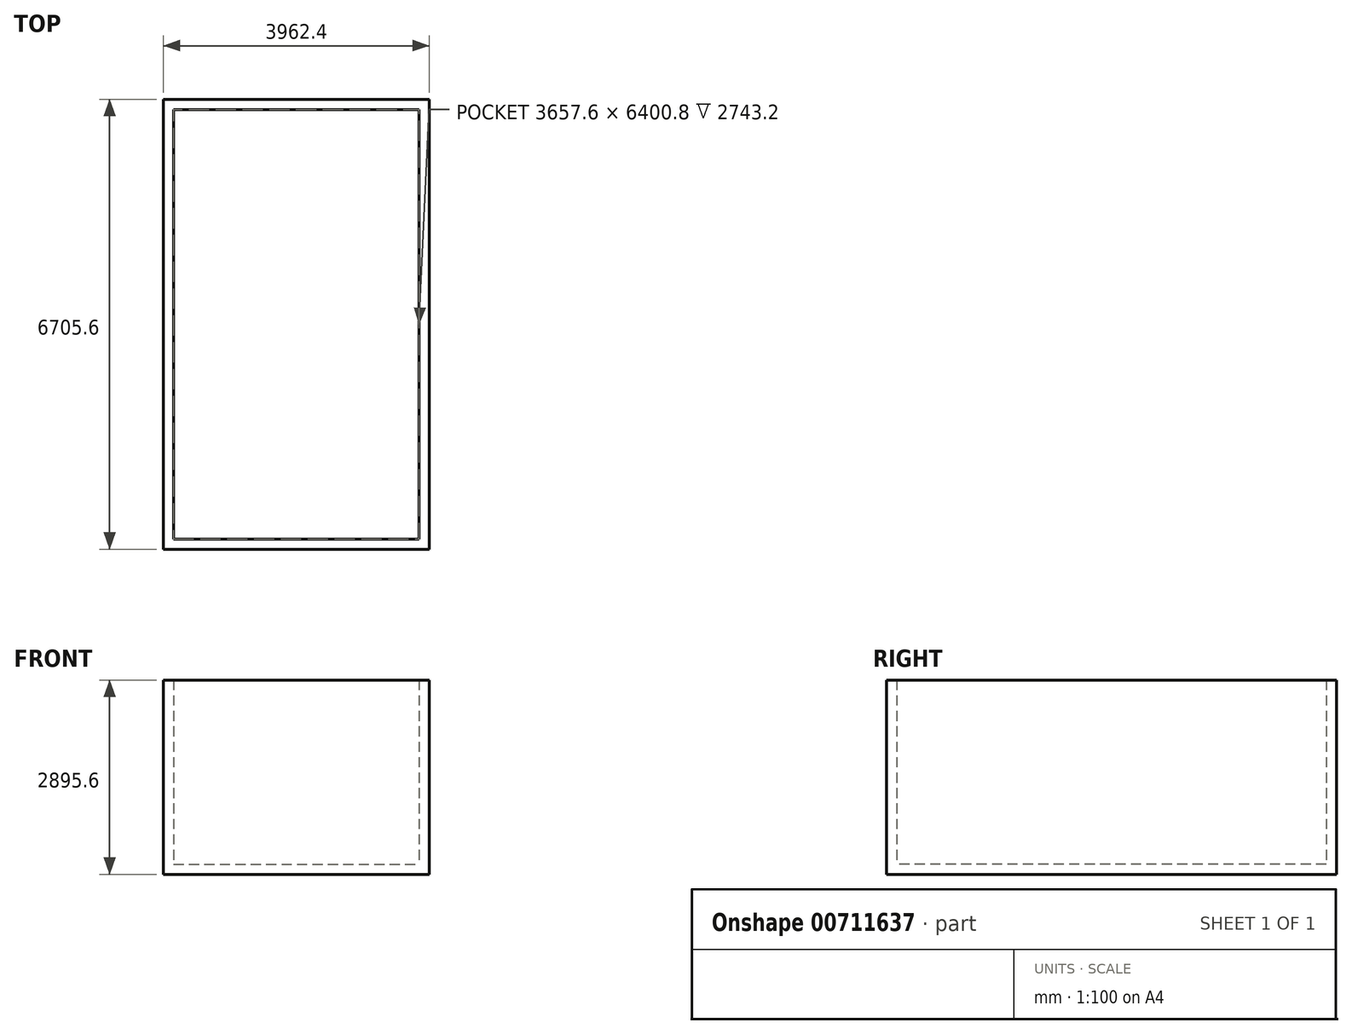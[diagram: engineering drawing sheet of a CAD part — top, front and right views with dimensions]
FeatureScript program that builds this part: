
annotation { "Feature Type Name" : "Feature", "Feature Type Description" : "" }
export const myFeature = defineFeature(function(context is Context, id is Id, definition is map)
    precondition{}
    {
        {
            var Q0;
            Q0=qCreatedBy(makeId("Top.planeOp"),FACE);
            var sketch = newSketch(context, id + "F0", { "sketchPlane" : qUnion([Q0])});
            skLineSegment(sketch, "E0.bottom", {"start": v(-1812.58, 3350.54) * mm, "end": v(1845.02, 3350.54) * mm});
            skLineSegment(sketch, "E0.top", {"start": v(-1812.58, -3050.26) * mm, "end": v(1845.02, -3050.26) * mm});
            skLineSegment(sketch, "E0.left", {"start": v(-1812.58, 3350.54) * mm, "end": v(-1812.58, -3050.26) * mm});
            skLineSegment(sketch, "E0.right", {"start": v(1845.02, 3350.54) * mm, "end": v(1845.02, -3050.26) * mm});
            skLineSegment(sketch, "E1.0", {"start": v(-1964.98, 3502.94) * mm, "end": v(-1964.98, -3202.66) * mm});
            skLineSegment(sketch, "E1.1", {"start": v(-1964.98, 3502.94) * mm, "end": v(1997.42, 3502.94) * mm});
            skLineSegment(sketch, "E1.2", {"start": v(1997.42, 3502.94) * mm, "end": v(1997.42, -3202.66) * mm});
            skLineSegment(sketch, "E1.3", {"start": v(-1964.98, -3202.66) * mm, "end": v(1997.42, -3202.66) * mm});
            skSolve(sketch);
        }
        {
            var Q0;
            Q0 = qSketchRegion(id + "F0", true);
            extrude(context, id + "F1", {"entities" : qUnion([Q0]), "depth" : 2743.2 * mm, "offsetDistance" : 25.4 * mm});
        }
        {
            var Q0;
            Q0=makeQuery(id+"F1.opExtrude","CAP_FACE",FACE,{"disambiguationData":[OSD([sQuery(id+"F0.wireOp",EDGE,"E0.bottom"),sQuery(id+"F0.wireOp",EDGE,"E0.top"),sQuery(id+"F0.wireOp",EDGE,"E0.left"),sQuery(id+"F0.wireOp",EDGE,"E0.right"),sQuery(id+"F0.wireOp",EDGE,"E1.0"),sQuery(id+"F0.wireOp",EDGE,"E1.1"),sQuery(id+"F0.wireOp",EDGE,"E1.2"),sQuery(id+"F0.wireOp",EDGE,"E1.3")])],"isStart":true});
            var sketch = newSketch(context, id + "F2", { "sketchPlane" : qUnion([Q0])});
            skLineSegment(sketch, "E2.0", {"start": v(-1964.98, -3502.94) * mm, "end": v(-1964.98, 3202.66) * mm});
            skLineSegment(sketch, "E3.0", {"start": v(-1964.98, -3502.94) * mm, "end": v(1997.42, -3502.94) * mm});
            skLineSegment(sketch, "E4.0", {"start": v(1997.42, -3502.94) * mm, "end": v(1997.42, 3202.66) * mm});
            skLineSegment(sketch, "E5.0.0", {"start": v(-1964.98, 3202.66) * mm, "end": v(1997.42, 3202.66) * mm});
            skLineSegment(sketch, "E5.0.2", {"start": v(1997.42, 3202.66) * mm, "end": v(-1964.98, 3202.66) * mm});
            skSolve(sketch);
        }
        {
            var Q0;
            Q0 = qSketchRegion(id + "F2", true);
            extrude(context, id + "F3", {"entities" : qUnion([Q0]), "operationType" : NewBodyOperationType.ADD, "depth" : 152.4 * mm, "offsetDistance" : 25.4 * mm});
        }
    });
